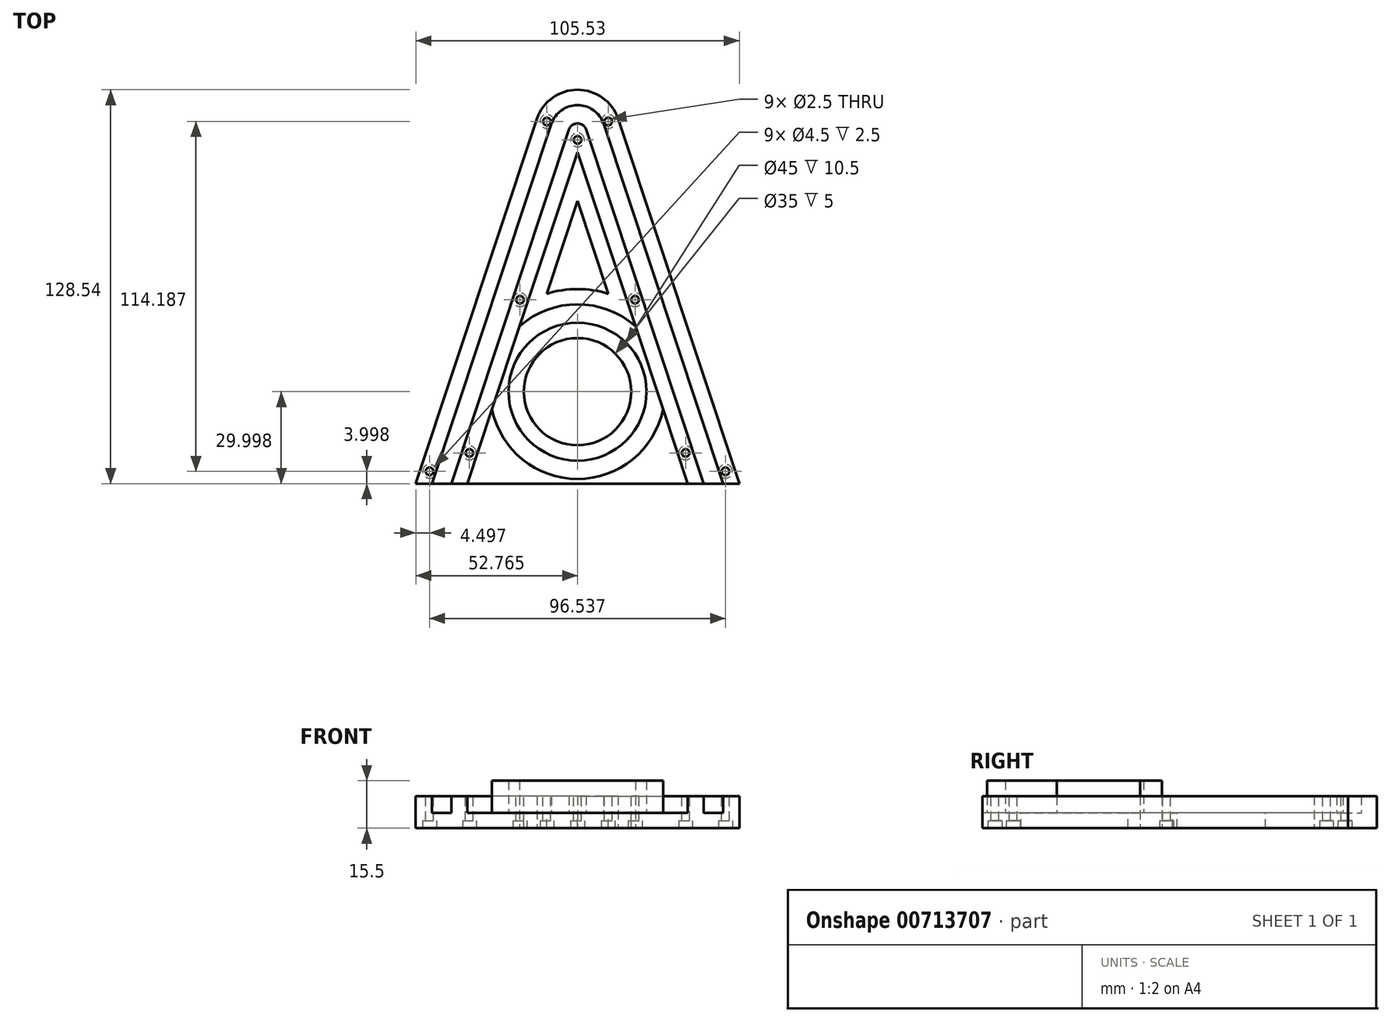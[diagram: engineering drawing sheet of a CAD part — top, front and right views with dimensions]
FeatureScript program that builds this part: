
annotation { "Feature Type Name" : "Feature", "Feature Type Description" : "" }
export const myFeature = defineFeature(function(context is Context, id is Id, definition is map)
    precondition{}
    {
        {
            var Q0;
            Q0=qCreatedBy(makeId("Top.planeOp"),FACE);
            var sketch = newSketch(context, id + "F0", { "sketchPlane" : qUnion([Q0])});
            skLineSegment(sketch, "E0.bottom", {"start": v(55.99, -14.54) * mm, "end": v(-39.01, -14.54) * mm});
            skLineSegment(sketch, "E1", {"start": v(0, 103) * mm, "end": v(-39.01, -14.54) * mm});
            skLineSegment(sketch, "E2", {"start": v(16.97, 103) * mm, "end": v(55.99, -14.54) * mm});
            skArc(sketch, "E3", {"start": v(16.97, 103) * mm, "mid": v(8.49, 109) * mm, "end": v(0, 103) * mm});
            skPoint(sketch, "E4", {"position": v(8.49, -14.54) * mm});
            skLineSegment(sketch, "E5.0", {"start": v(-4.73, 104.62) * mm, "end": v(-44.28, -14.54) * mm});
            skArc(sketch, "E5.1", {"start": v(21.7, 104.62) * mm, "mid": v(8.49, 114) * mm, "end": v(-4.73, 104.62) * mm});
            skLineSegment(sketch, "E5.2", {"start": v(21.7, 104.62) * mm, "end": v(61.25, -14.54) * mm});
            skLineSegment(sketch, "E6", {"start": v(-39.01, -14.54) * mm, "end": v(-44.28, -14.54) * mm});
            skLineSegment(sketch, "E7", {"start": v(55.99, -14.54) * mm, "end": v(61.25, -14.54) * mm});
            skLineSegment(sketch, "E8.0", {"start": v(12.24, 101.37) * mm, "end": v(50.72, -14.54) * mm});
            skArc(sketch, "E8.1", {"start": v(12.24, 101.37) * mm, "mid": v(8.49, 104) * mm, "end": v(4.73, 101.37) * mm});
            skLineSegment(sketch, "E8.2", {"start": v(4.73, 101.37) * mm, "end": v(-33.75, -14.54) * mm});
            skSolve(sketch);
        }
        {
            var Q0;
            Q0 = qSketchRegion(id + "F0", true);
            extrude(context, id + "F1", {"entities" : qUnion([Q0]), "depth" : 5 * mm, "offsetDistance" : 25 * mm});
        }
        {
            var Q0;
            Q0=makeQuery(id+"F1.opExtrude","CAP_FACE",FACE,{"disambiguationData":[OSD([sQuery(id+"F0.wireOp",EDGE,"E0.bottom"),sQuery(id+"F0.wireOp",EDGE,"E5.0"),sQuery(id+"F0.wireOp",EDGE,"E5.1"),sQuery(id+"F0.wireOp",EDGE,"E5.2"),sQuery(id+"F0.wireOp",EDGE,"E6"),sQuery(id+"F0.wireOp",EDGE,"E7")])],"isStart":false});
            var sketch = newSketch(context, id + "F2", { "sketchPlane" : qUnion([Q0])});
            skLineSegment(sketch, "E9.0", {"start": v(0, 103) * mm, "end": v(-39.01, -14.54) * mm});
            skArc(sketch, "E9.1", {"start": v(16.97, 103) * mm, "mid": v(8.49, 109) * mm, "end": v(0, 103) * mm});
            skLineSegment(sketch, "E9.2", {"start": v(16.97, 103) * mm, "end": v(55.99, -14.54) * mm});
            skSolve(sketch);
        }
        {
            var Q0;
            Q0 = qSketchRegion(id + "F2", true);
            var Q1;
            {var subQ2=sQuery(id+"F2.wireOp",EDGE,"E9.0");Q1=makeQuery(id+"F2.imprint","IMPRINT",FACE,{"disambiguationData":[TD([[makeQuery(id+"F2.imprint","IMPRINT",EDGE,{"derivedFrom":subQ2}),-1.0]])]});}
            extrude(context, id + "F3", {"entities" : qUnion([Q0, Q1]), "operationType" : NewBodyOperationType.ADD, "depth" : 5.5 * mm, "offsetDistance" : 25 * mm});
        }
        {
            var Q0;
            Q0=makeQuery(id+"F1.opExtrude","CAP_FACE",FACE,{"disambiguationData":[OSD([sQuery(id+"F0.wireOp",EDGE,"E0.bottom"),sQuery(id+"F0.wireOp",EDGE,"E5.0"),sQuery(id+"F0.wireOp",EDGE,"E5.1"),sQuery(id+"F0.wireOp",EDGE,"E5.2"),sQuery(id+"F0.wireOp",EDGE,"E6"),sQuery(id+"F0.wireOp",EDGE,"E7")])],"isStart":false});
            var sketch = newSketch(context, id + "F4", { "sketchPlane" : qUnion([Q0])});
            skLineSegment(sketch, "E10.0", {"start": v(5.67, 101.04) * mm, "end": v(-32.7, -14.54) * mm});
            skArc(sketch, "E10.1", {"start": v(11.3, 101.04) * mm, "mid": v(8.49, 103) * mm, "end": v(5.67, 101.04) * mm});
            skLineSegment(sketch, "E10.2", {"start": v(11.3, 101.04) * mm, "end": v(49.66, -14.54) * mm});
            skLineSegment(sketch, "E11.0", {"start": v(8.49, 93.65) * mm, "end": v(-27.42, -14.54) * mm});
            skLineSegment(sketch, "E11.1", {"start": v(8.49, 93.65) * mm, "end": v(44.4, -14.54) * mm});
            skSolve(sketch);
        }
        {
            var Q0;
            {var subQ2=sQuery(id+"F4.wireOp",EDGE,"E10.0");Q0=makeQuery(id+"F4.imprint","IMPRINT",FACE,{"disambiguationData":[TD([[makeQuery(id+"F4.imprint","IMPRINT",EDGE,{"derivedFrom":subQ2}),1.0]])]});}
            extrude(context, id + "F5", {"entities" : qUnion([Q0]), "operationType" : NewBodyOperationType.ADD, "depth" : 5.5 * mm, "offsetDistance" : 25 * mm});
        }
        {
            var Q0;
            {var subQ0=sQuery(id+"F0.wireOp",EDGE,"E5.0");var subQ1=sQuery(id+"F0.wireOp",EDGE,"E7");var subQ2=sQuery(id+"F0.wireOp",EDGE,"E6");var subQ3=sQuery(id+"F0.wireOp",EDGE,"E0.bottom");var subQ5=sQuery(id+"F4.wireOp",EDGE,"E11.0");var subQ6=sQuery(id+"F0.wireOp",EDGE,"E5.2");Q0=makeQuery(id+"F5.boolean.opBoolean","SPLIT",FACE,{"disambiguationData":[TD([makeQuery(id+"F5.opExtrude","SWEPT_FACE",FACE,{"disambiguationData":[OSD([subQ5])]})])],"derivedFrom":makeQuery(id+"F1.opExtrude","CAP_FACE",FACE,{"disambiguationData":[OSD([subQ3,subQ0,sQuery(id+"F0.wireOp",EDGE,"E5.1"),subQ6,subQ2,subQ1])],"isStart":false})});}
            var sketch = newSketch(context, id + "F6", { "sketchPlane" : qUnion([Q0])});
            skCircle(sketch, "E12", {"center": v(8.49, 15.46) * mm, "radius": 22.5 * mm});
            skCircle(sketch, "E13.0", {"center": v(8.49, 15.46) * mm, "radius": 28.5 * mm});
            skSolve(sketch);
        }
        {
            var Q0;
            Q0=makeQuery(id+"F6.imprint","IMPRINT",FACE,{"disambiguationData":[TD([[makeQuery(id+"F6.imprint","IMPRINT",EDGE,{"derivedFrom":sQuery(id+"F6.wireOp",EDGE,"E12")}),-1.0]])]});
            extrude(context, id + "F7", {"entities" : qUnion([Q0]), "operationType" : NewBodyOperationType.ADD, "depth" : 10.5 * mm, "offsetDistance" : 25 * mm});
        }
        {
            var Q0;
            {var subQ0=sQuery(id+"F0.wireOp",EDGE,"E5.0");var subQ1=sQuery(id+"F0.wireOp",EDGE,"E7");var subQ2=sQuery(id+"F0.wireOp",EDGE,"E6");var subQ3=sQuery(id+"F0.wireOp",EDGE,"E0.bottom");var subQ5=sQuery(id+"F4.wireOp",EDGE,"E11.0");var subQ6=sQuery(id+"F0.wireOp",EDGE,"E5.2");Q0=makeQuery(id+"F7.boolean.opBoolean","SPLIT",FACE,{"disambiguationData":[TD([makeQuery(id+"F7.opExtrude","SWEPT_FACE",FACE,{"disambiguationData":[OSD([sQuery(id+"F6.wireOp",EDGE,"E12")])]})])],"derivedFrom":makeQuery(id+"F5.boolean.opBoolean","SPLIT",FACE,{"disambiguationData":[TD([makeQuery(id+"F5.opExtrude","SWEPT_FACE",FACE,{"disambiguationData":[OSD([subQ5])]})])],"derivedFrom":makeQuery(id+"F1.opExtrude","CAP_FACE",FACE,{"disambiguationData":[OSD([subQ3,subQ0,sQuery(id+"F0.wireOp",EDGE,"E5.1"),subQ6,subQ2,subQ1])],"isStart":false})})});}
            var sketch = newSketch(context, id + "F8", { "sketchPlane" : qUnion([Q0])});
            skCircle(sketch, "E14", {"center": v(8.49, 15.46) * mm, "radius": 17.5 * mm});
            skSolve(sketch);
        }
        {
            var Q0;
            Q0 = qSketchRegion(id + "F8", true);
            extrude(context, id + "F9", {"entities" : qUnion([Q0]), "operationType" : NewBodyOperationType.REMOVE, "oppositeDirection" : true, "depth" : 25 * mm, "offsetDistance" : 25 * mm});
        }
        {
            var Q0;
            {var subQ0=sQuery(id+"F4.wireOp",EDGE,"E11.0");var subQ1=makeQuery(id+"F5.opExtrude","SWEPT_FACE",FACE,{"disambiguationData":[OSD([subQ0])]});var subQ4=sQuery(id+"F6.wireOp",EDGE,"E13.0");var subQ5=sQuery(id+"F0.wireOp",EDGE,"E5.0");var subQ6=sQuery(id+"F0.wireOp",EDGE,"E7");var subQ7=sQuery(id+"F0.wireOp",EDGE,"E6");var subQ8=sQuery(id+"F0.wireOp",EDGE,"E0.bottom");var subQ10=sQuery(id+"F0.wireOp",EDGE,"E5.2");Q0=makeQuery(id+"F7.boolean.opBoolean","SPLIT",FACE,{"disambiguationData":[TD([makeQuery(id+"F7.opExtrude","SWEPT_FACE",FACE,{"disambiguationData":[OSD([subQ4]),TDD([makeQuery(id+"F6.imprint","IMPRINT",EDGE,{"disambiguationData":[TD([[makeQuery(id+"F6.imprint","INTERSECT",VERTEX,{"disambiguationData":[OD(0.0)],"derivedFrom":[makeQuery(id+"F5.opExtrude","CAP_EDGE",EDGE,{"disambiguationData":[OSD([subQ0])],"isStart":true}),subQ4]}),1.0]])],"derivedFrom":subQ4})])]})])],"derivedFrom":makeQuery(id+"F5.boolean.opBoolean","SPLIT",FACE,{"disambiguationData":[TD([subQ1])],"derivedFrom":makeQuery(id+"F1.opExtrude","CAP_FACE",FACE,{"disambiguationData":[OSD([subQ8,subQ5,sQuery(id+"F0.wireOp",EDGE,"E5.1"),subQ10,subQ7,subQ6])],"isStart":false})})});}
            var sketch = newSketch(context, id + "F10", { "sketchPlane" : qUnion([Q0])});
            skArc(sketch, "E15.0", {"start": v(-1.6, 47.4) * mm, "mid": v(8.49, 48.96) * mm, "end": v(18.57, 47.4) * mm});
            skLineSegment(sketch, "E15.1", {"start": v(8.49, 77.77) * mm, "end": v(-1.6, 47.4) * mm});
            skLineSegment(sketch, "E15.2", {"start": v(18.57, 47.4) * mm, "end": v(8.49, 77.77) * mm});
            skSolve(sketch);
        }
        {
            var Q0;
            Q0=makeQuery(id+"F10.imprint","IMPRINT",FACE,{"disambiguationData":[TD([[makeQuery(id+"F10.imprint","IMPRINT",EDGE,{"derivedFrom":sQuery(id+"F10.wireOp",EDGE,"E15.0")}),1.0]])]});
            extrude(context, id + "F11", {"entities" : qUnion([Q0]), "operationType" : NewBodyOperationType.REMOVE, "oppositeDirection" : true, "depth" : 25 * mm, "offsetDistance" : 25 * mm});
        }
        {
            var Q0;
            Q0=makeQuery(id+"F5.opExtrude","CAP_FACE",FACE,{"disambiguationData":[OSD([sQuery(id+"F0.wireOp",EDGE,"E0.bottom"),sQuery(id+"F0.wireOp",EDGE,"E6"),sQuery(id+"F0.wireOp",EDGE,"E7"),sQuery(id+"F4.wireOp",EDGE,"E10.0"),sQuery(id+"F4.wireOp",EDGE,"E10.1"),sQuery(id+"F4.wireOp",EDGE,"E10.2"),sQuery(id+"F4.wireOp",EDGE,"E11.0"),sQuery(id+"F4.wireOp",EDGE,"E11.1")])],"isStart":false});
            var sketch = newSketch(context, id + "F12", { "sketchPlane" : qUnion([Q0])});
            skCircle(sketch, "E16", {"center": v(8.5, 97.65) * mm, "radius": 1.25 * mm});
            skCircle(sketch, "E17", {"center": v(-1.51, 103.65) * mm, "radius": 1.25 * mm});
            skCircle(sketch, "E18", {"center": v(18.49, 103.65) * mm, "radius": 1.25 * mm});
            skCircle(sketch, "E19", {"center": v(-10.28, 45.46) * mm, "radius": 1.25 * mm});
            skCircle(sketch, "E20", {"center": v(27.25, 45.46) * mm, "radius": 1.25 * mm});
            skCircle(sketch, "E21", {"center": v(56.75, -10.54) * mm, "radius": 1.25 * mm});
            skCircle(sketch, "E22", {"center": v(43.75, -4.54) * mm, "radius": 1.25 * mm});
            skCircle(sketch, "E23", {"center": v(-26.78, -4.54) * mm, "radius": 1.25 * mm});
            skCircle(sketch, "E24", {"center": v(-39.78, -10.54) * mm, "radius": 1.25 * mm});
            skSolve(sketch);
        }
        {
            var Q0;
            Q0 = qSketchRegion(id + "F12", true);
            extrude(context, id + "F13", {"entities" : qUnion([Q0]), "operationType" : NewBodyOperationType.REMOVE, "oppositeDirection" : true, "depth" : 11 * mm, "offsetDistance" : 25 * mm});
        }
        {
            var Q0;
            Q0=makeQuery(id+"F1.opExtrude","CAP_FACE",FACE,{"disambiguationData":[OSD([sQuery(id+"F0.wireOp",EDGE,"E0.bottom"),sQuery(id+"F0.wireOp",EDGE,"E5.0"),sQuery(id+"F0.wireOp",EDGE,"E5.1"),sQuery(id+"F0.wireOp",EDGE,"E5.2"),sQuery(id+"F0.wireOp",EDGE,"E6"),sQuery(id+"F0.wireOp",EDGE,"E7")])],"isStart":true});
            var sketch = newSketch(context, id + "F14", { "sketchPlane" : qUnion([Q0])});
            skCircle(sketch, "E25", {"center": v(18.49, -103.65) * mm, "radius": 2.25 * mm});
            skCircle(sketch, "E26", {"center": v(8.5, -97.65) * mm, "radius": 2.25 * mm});
            skCircle(sketch, "E27", {"center": v(-1.51, -103.65) * mm, "radius": 2.25 * mm});
            skCircle(sketch, "E28", {"center": v(-10.28, -45.46) * mm, "radius": 2.25 * mm});
            skCircle(sketch, "E29", {"center": v(27.25, -45.46) * mm, "radius": 2.25 * mm});
            skCircle(sketch, "E30", {"center": v(-39.78, 10.54) * mm, "radius": 2.25 * mm});
            skCircle(sketch, "E31", {"center": v(-26.78, 4.54) * mm, "radius": 2.25 * mm});
            skCircle(sketch, "E32", {"center": v(43.75, 4.54) * mm, "radius": 2.25 * mm});
            skCircle(sketch, "E33", {"center": v(56.75, 10.54) * mm, "radius": 2.25 * mm});
            skSolve(sketch);
        }
        {
            var Q0;
            Q0 = qSketchRegion(id + "F14", true);
            extrude(context, id + "F15", {"entities" : qUnion([Q0]), "operationType" : NewBodyOperationType.REMOVE, "oppositeDirection" : true, "depth" : 2.5 * mm, "offsetDistance" : 25 * mm});
        }
    });
